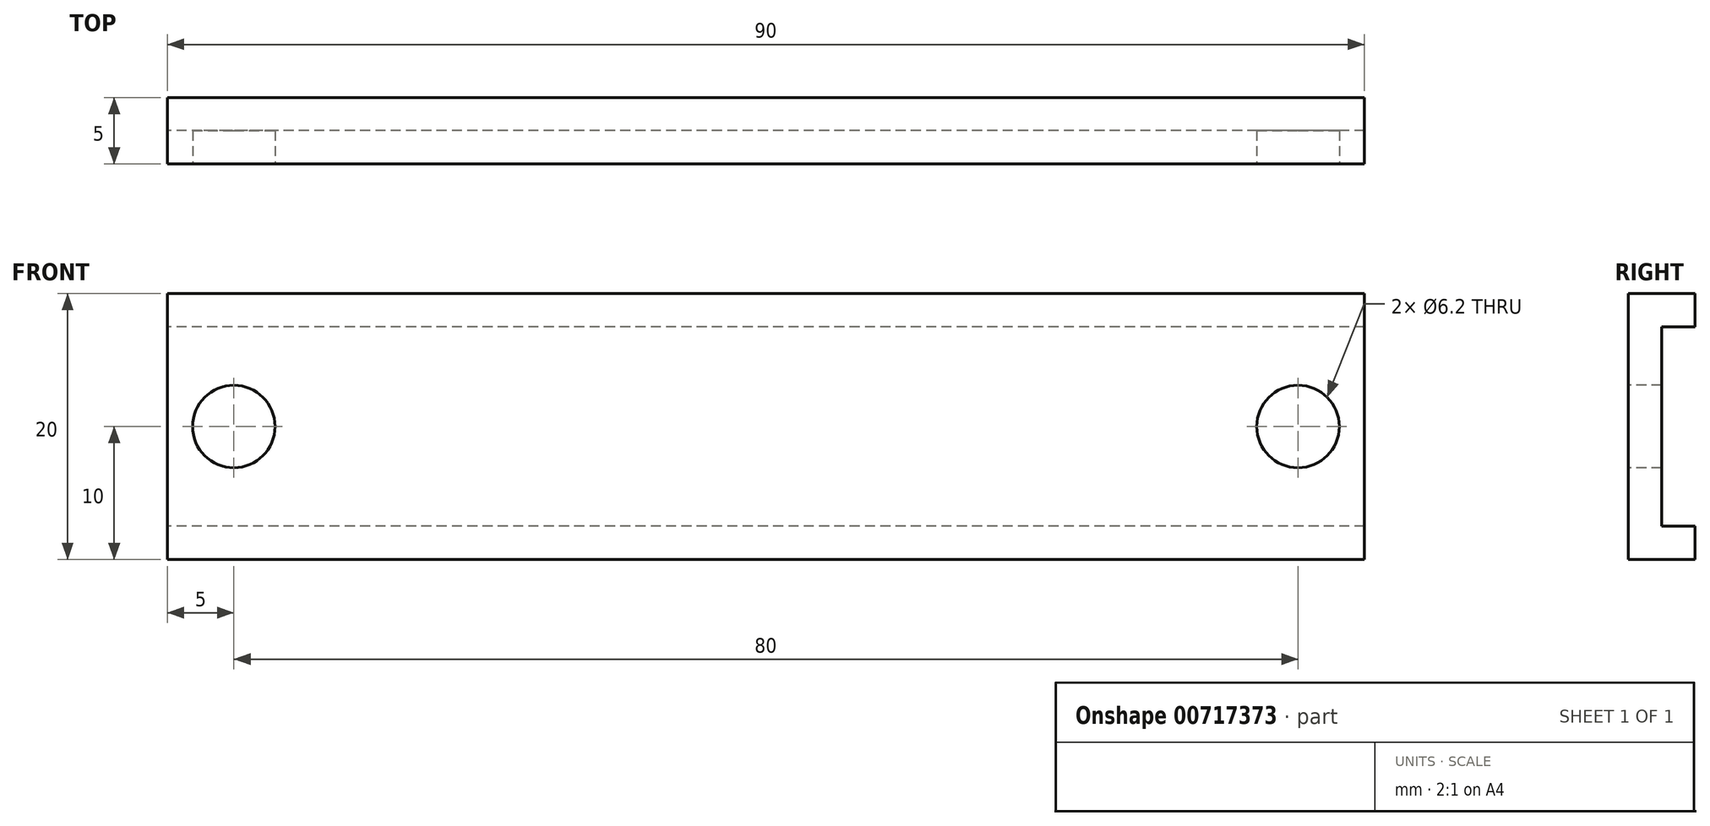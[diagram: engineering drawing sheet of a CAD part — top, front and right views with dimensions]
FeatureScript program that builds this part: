
annotation { "Feature Type Name" : "Feature", "Feature Type Description" : "" }
export const myFeature = defineFeature(function(context is Context, id is Id, definition is map)
    precondition{}
    {
        {
            var Q0;
            Q0=qCreatedBy(makeId("Front.planeOp"),FACE);
            var sketch = newSketch(context, id + "F0", { "sketchPlane" : qUnion([Q0])});
            skLineSegment(sketch, "E0.bottom", {"start": v(45, 10) * mm, "end": v(-45, 10) * mm});
            skLineSegment(sketch, "E0.top", {"start": v(45, -10) * mm, "end": v(-45, -10) * mm});
            skLineSegment(sketch, "E0.left", {"start": v(45, 10) * mm, "end": v(45, -10) * mm});
            skLineSegment(sketch, "E0.right", {"start": v(-45, 10) * mm, "end": v(-45, -10) * mm});
            skPoint(sketch, "E0.middle", {"position": v(0, 0) * mm});
            skSolve(sketch);
        }
        {
            var Q0;
            Q0=makeQuery(id+"F0.imprint","IMPRINT",FACE,{"disambiguationData":[TD([[makeQuery(id+"F0.imprint","IMPRINT",EDGE,{"derivedFrom":sQuery(id+"F0.wireOp",EDGE,"E0.bottom")}),1.0]])]});
            extrude(context, id + "F1", {"entities" : qUnion([Q0]), "depth" : 5 * mm, "offsetDistance" : 25 * mm});
        }
        {
            var Q0;
            Q0=makeQuery(id+"F1.opExtrude","CAP_FACE",FACE,{"disambiguationData":[OSD([sQuery(id+"F0.wireOp",EDGE,"E0.bottom"),sQuery(id+"F0.wireOp",EDGE,"E0.top"),sQuery(id+"F0.wireOp",EDGE,"E0.left"),sQuery(id+"F0.wireOp",EDGE,"E0.right")])],"isStart":true});
            var Q1;
            Q1=makeQuery(id+"F1.opExtrude","SWEPT_FACE",FACE,{"disambiguationData":[OSD([sQuery(id+"F0.wireOp",EDGE,"E0.left")])]});
            var Q2;
            Q2=makeQuery(id+"F1.opExtrude","SWEPT_FACE",FACE,{"disambiguationData":[OSD([sQuery(id+"F0.wireOp",EDGE,"E0.right")])]});
            shell(context, id + "F2", {"entities" : qUnion([Q0, Q1, Q2]), "thickness" : 2.5 * mm});
        }
        {
            var Q0;
            Q0=makeQuery(id+"F1.opExtrude","CAP_FACE",FACE,{"disambiguationData":[OSD([sQuery(id+"F0.wireOp",EDGE,"E0.bottom"),sQuery(id+"F0.wireOp",EDGE,"E0.top"),sQuery(id+"F0.wireOp",EDGE,"E0.left"),sQuery(id+"F0.wireOp",EDGE,"E0.right")])],"isStart":false});
            var sketch = newSketch(context, id + "F3", { "sketchPlane" : qUnion([Q0])});
            skPoint(sketch, "E1", {"position": v(-40, 0) * mm});
            skPoint(sketch, "E2", {"position": v(40, 0) * mm});
            skSolve(sketch);
        }
        {
            var Q0;
            Q0=sQuery(id+"F3.wireOp",VERTEX,"E2");
            var Q1;
            Q1=sQuery(id+"F3.wireOp",VERTEX,"E1");
            var Q2;
            Q2=makeQuery(id+"F1.opExtrude","SWEPT_BODY",BODY,{"disambiguationData":[OSD([sQuery(id+"F0.wireOp",EDGE,"E0.bottom"),sQuery(id+"F0.wireOp",EDGE,"E0.top"),sQuery(id+"F0.wireOp",EDGE,"E0.left"),sQuery(id+"F0.wireOp",EDGE,"E0.right")])]});
            hole(context, id + "F4", {"style" : HoleStyle.SIMPLE, "endStyle" : HoleEndStyle.THROUGH, "holeDiameter" : 6.2 * mm, "majorDiameter" : 5 * mm, "isTappedThrough" : true, "tappedDepth" : 12 * mm, "tapClearance" : 3, "locations" : qUnion([Q0, Q1]), "scope" : qUnion([Q2])});
        }
    });
